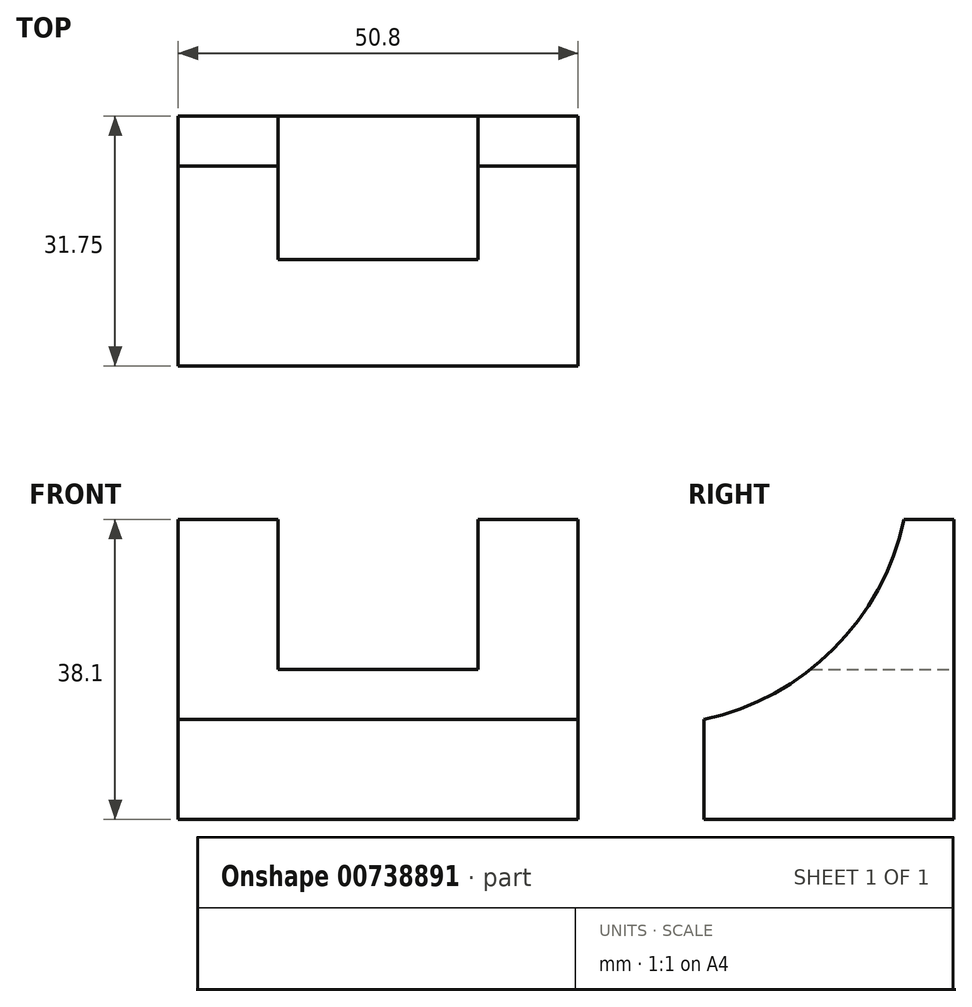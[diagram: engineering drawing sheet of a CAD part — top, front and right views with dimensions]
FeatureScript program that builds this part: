
annotation { "Feature Type Name" : "Feature", "Feature Type Description" : "" }
export const myFeature = defineFeature(function(context is Context, id is Id, definition is map)
    precondition{}
    {
        {
            var Q0;
            Q0=qCreatedBy(makeId("Front.planeOp"),FACE);
            var sketch = newSketch(context, id + "F0", { "sketchPlane" : qUnion([Q0])});
            skLineSegment(sketch, "E0", {"start": v(0, 38.1) * mm, "end": v(0, 0) * mm});
            skLineSegment(sketch, "E1", {"start": v(0, 0) * mm, "end": v(50.8, 0) * mm});
            skLineSegment(sketch, "E2", {"start": v(50.8, 0) * mm, "end": v(50.8, 38.1) * mm});
            skLineSegment(sketch, "E3", {"start": v(50.8, 38.1) * mm, "end": v(0, 38.1) * mm});
            skSolve(sketch);
        }
        {
            var Q0;
            Q0 = qSketchRegion(id + "F0", true);
            var Q1;
            Q1=makeQuery(id+"F0.imprint","IMPRINT",FACE,{"disambiguationData":[TD([[makeQuery(id+"F0.imprint","IMPRINT",EDGE,{"derivedFrom":sQuery(id+"F0.wireOp",EDGE,"E0")}),1.0]])]});
            extrude(context, id + "F1", {"entities" : qUnion([Q0, Q1]), "depth" : 31.75 * mm, "offsetDistance" : 25.4 * mm});
        }
        {
            var Q0;
            Q0=makeQuery(id+"F1.opExtrude","SWEPT_FACE",FACE,{"disambiguationData":[OSD([sQuery(id+"F0.wireOp",EDGE,"E2")])]});
            var sketch = newSketch(context, id + "F2", { "sketchPlane" : qUnion([Q0])});
            skArc(sketch, "E4", {"start": v(-31.75, 12.7) * mm, "mid": v(-15.3, 21.65) * mm, "end": v(-6.35, 38.1) * mm});
            skSolve(sketch);
        }
        {
            var Q0;
            {var subQ0=sQuery(id+"F2.wireOp",EDGE,"E4");Q0=makeQuery(id+"F2.imprint","IMPRINT",FACE,{"disambiguationData":[TD([[makeQuery(id+"F2.imprint","IMPRINT",EDGE,{"derivedFrom":subQ0}),1.0]])]});}
            extrude(context, id + "F3", {"entities" : qUnion([Q0]), "operationType" : NewBodyOperationType.REMOVE, "endBound" : BoundingType.THROUGH_ALL, "oppositeDirection" : true, "depth" : 25.4 * mm, "offsetDistance" : 25.4 * mm});
        }
        {
            var Q0;
            Q0=makeQuery(id+"F1.opExtrude","CAP_FACE",FACE,{"disambiguationData":[OSD([sQuery(id+"F0.wireOp",EDGE,"E0"),sQuery(id+"F0.wireOp",EDGE,"E1"),sQuery(id+"F0.wireOp",EDGE,"E2"),sQuery(id+"F0.wireOp",EDGE,"E3")])],"isStart":true});
            var sketch = newSketch(context, id + "F4", { "sketchPlane" : qUnion([Q0])});
            skLineSegment(sketch, "E5", {"start": v(-38.1, 38.1) * mm, "end": v(-38.1, 19.05) * mm});
            skLineSegment(sketch, "E6", {"start": v(-38.1, 19.05) * mm, "end": v(-12.7, 19.05) * mm});
            skLineSegment(sketch, "E7", {"start": v(-12.7, 19.05) * mm, "end": v(-12.7, 38.1) * mm});
            skSolve(sketch);
        }
        {
            var Q0;
            Q0 = qSketchRegion(id + "F4", true);
            var Q1;
            {var subQ0=sQuery(id+"F4.wireOp",EDGE,"E5");Q1=makeQuery(id+"F4.imprint","IMPRINT",FACE,{"disambiguationData":[TD([[makeQuery(id+"F4.imprint","IMPRINT",EDGE,{"derivedFrom":subQ0}),1.0]])]});}
            extrude(context, id + "F5", {"entities" : qUnion([Q0, Q1]), "operationType" : NewBodyOperationType.REMOVE, "endBound" : BoundingType.THROUGH_ALL, "oppositeDirection" : true, "depth" : 25.4 * mm, "offsetDistance" : 25.4 * mm});
        }
    });
